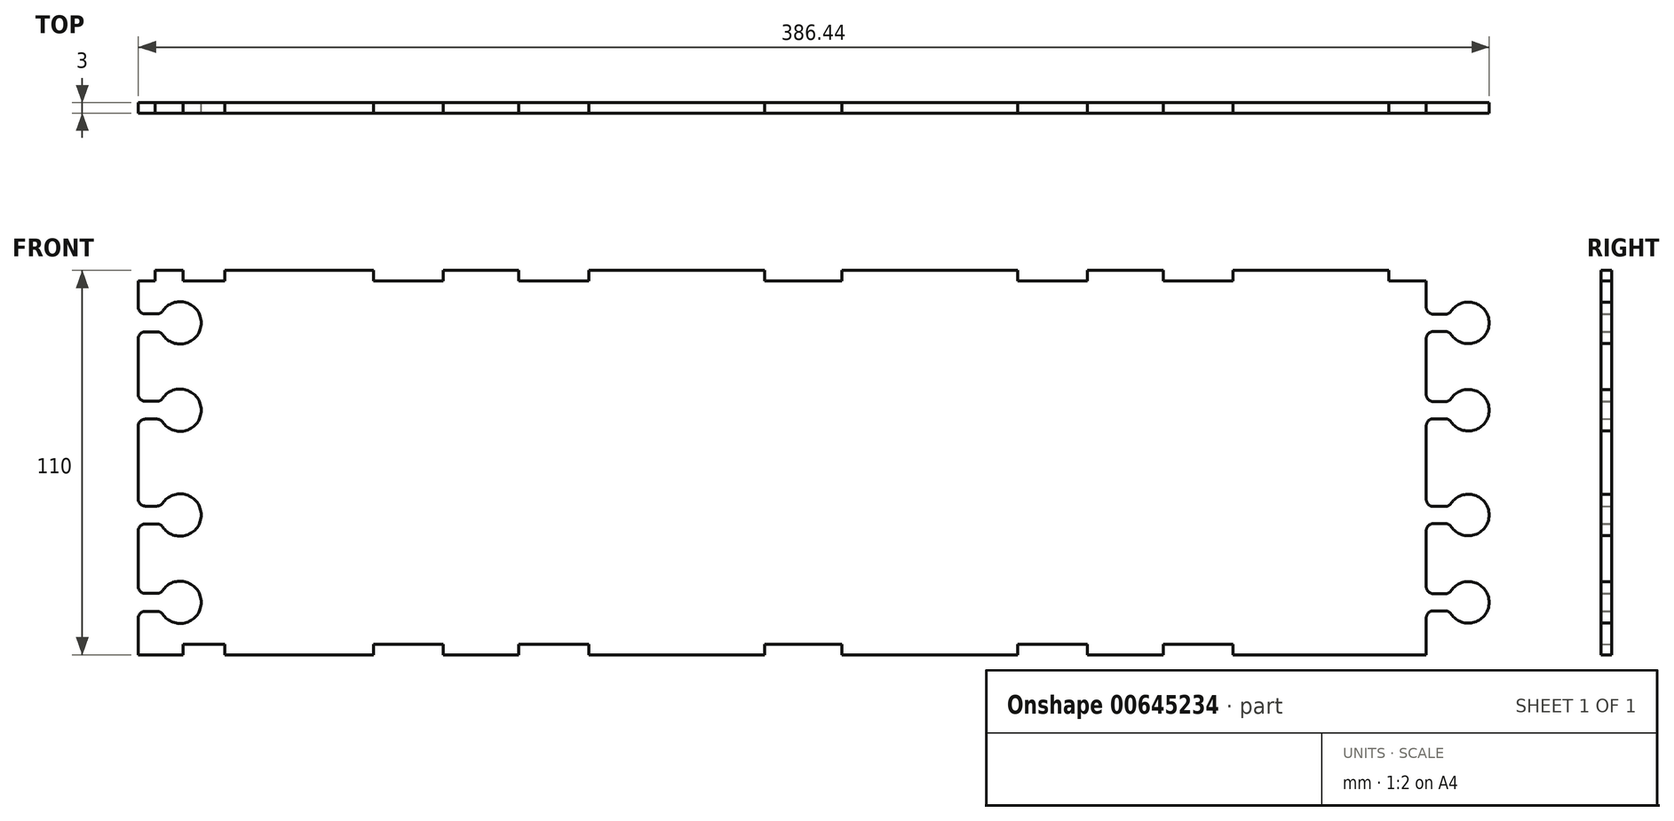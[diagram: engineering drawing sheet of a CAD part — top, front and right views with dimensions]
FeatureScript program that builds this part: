
annotation { "Feature Type Name" : "Feature", "Feature Type Description" : "" }
export const myFeature = defineFeature(function(context is Context, id is Id, definition is map)
    precondition{}
    {
        {
            var Q0;
            Q0=qCreatedBy(makeId("Front.planeOp"),FACE);
            var sketch = newSketch(context, id + "F0", { "sketchPlane" : qUnion([Q0])});
            skLineSegment(sketch, "E0", {"start": v(142.7, 55) * mm, "end": v(142.7, -55) * mm});
            skLineSegment(sketch, "E1", {"start": v(52.34, 55) * mm, "end": v(18.8, 55) * mm});
            skLineSegment(sketch, "E2", {"start": v(18.8, 55) * mm, "end": v(18.8, -55) * mm});
            skLineSegment(sketch, "E3", {"start": v(18.8, -55) * mm, "end": v(52.34, -55) * mm});
            skLineSegment(sketch, "E4", {"start": v(-24.8, 55) * mm, "end": v(-58.34, 55) * mm});
            skLineSegment(sketch, "E5", {"start": v(159.47, 55) * mm, "end": v(125.94, 55) * mm});
            skLineSegment(sketch, "E6", {"start": v(-131.94, 55) * mm, "end": v(-165.47, 55) * mm});
            skLineSegment(sketch, "E7", {"start": v(-165.47, 55) * mm, "end": v(-165.47, -55) * mm});
            skLineSegment(sketch, "E8", {"start": v(-58.34, -55) * mm, "end": v(-24.8, -55) * mm});
            skLineSegment(sketch, "E9", {"start": v(-131.94, 55) * mm, "end": v(-131.94, -55) * mm});
            skLineSegment(sketch, "E10", {"start": v(125.94, 55) * mm, "end": v(125.94, -55) * mm});
            skLineSegment(sketch, "E11", {"start": v(-24.8, -55) * mm, "end": v(-14, -55) * mm});
            skLineSegment(sketch, "E12", {"start": v(159.47, 55) * mm, "end": v(159.47, -55) * mm});
            skLineSegment(sketch, "E13", {"start": v(52.34, 55) * mm, "end": v(52.34, -55) * mm});
            skLineSegment(sketch, "E14", {"start": v(8, -55) * mm, "end": v(8, -52) * mm});
            skLineSegment(sketch, "E15", {"start": v(-165.47, -55) * mm, "end": v(-131.94, -55) * mm});
            skLineSegment(sketch, "E16", {"start": v(8, 55) * mm, "end": v(18.8, 55) * mm});
            skLineSegment(sketch, "E17", {"start": v(-24.8, 55) * mm, "end": v(-24.8, -55) * mm});
            skLineSegment(sketch, "E18", {"start": v(-14, 52) * mm, "end": v(8, 52) * mm});
            skLineSegment(sketch, "E19", {"start": v(-14, 55) * mm, "end": v(-14, 52) * mm});
            skLineSegment(sketch, "E20", {"start": v(8, -52) * mm, "end": v(-14, -52) * mm});
            skLineSegment(sketch, "E21", {"start": v(-58.34, 55) * mm, "end": v(-58.34, -55) * mm});
            skLineSegment(sketch, "E22", {"start": v(-125.94, -52) * mm, "end": v(-125.94, -55) * mm});
            skLineSegment(sketch, "E23", {"start": v(8, 52) * mm, "end": v(8, 55) * mm});
            skLineSegment(sketch, "E24", {"start": v(-105.94, -52) * mm, "end": v(-125.94, -52) * mm});
            skLineSegment(sketch, "E25", {"start": v(-105.94, -55) * mm, "end": v(-105.94, -52) * mm});
            skLineSegment(sketch, "E26", {"start": v(-105.94, -55) * mm, "end": v(-84.34, -55) * mm});
            skLineSegment(sketch, "E27", {"start": v(-24.8, 55) * mm, "end": v(-14, 55) * mm});
            skLineSegment(sketch, "E28", {"start": v(-131.94, 55) * mm, "end": v(-125.94, 55) * mm});
            skLineSegment(sketch, "E29", {"start": v(8, -55) * mm, "end": v(18.8, -55) * mm});
            skLineSegment(sketch, "E30", {"start": v(125.94, -55) * mm, "end": v(159.47, -55) * mm});
            skLineSegment(sketch, "E31", {"start": v(-64.34, 55) * mm, "end": v(-58.34, 55) * mm});
            skLineSegment(sketch, "E32", {"start": v(-14, -52) * mm, "end": v(-14, -55) * mm});
            skLineSegment(sketch, "E33", {"start": v(-64.34, -52) * mm, "end": v(-84.34, -52) * mm});
            skLineSegment(sketch, "E34", {"start": v(-84.34, 55) * mm, "end": v(-84.34, 52) * mm});
            skLineSegment(sketch, "E35", {"start": v(-131.94, -55) * mm, "end": v(-125.94, -55) * mm});
            skLineSegment(sketch, "E36", {"start": v(-64.34, -55) * mm, "end": v(-64.34, -52) * mm});
            skLineSegment(sketch, "E37", {"start": v(-64.34, 52) * mm, "end": v(-64.34, 55) * mm});
            skLineSegment(sketch, "E38", {"start": v(164.47, 55) * mm, "end": v(164.47, 52) * mm});
            skLineSegment(sketch, "E39", {"start": v(-84.34, -52) * mm, "end": v(-84.34, -55) * mm});
            skLineSegment(sketch, "E40", {"start": v(-105.94, 55) * mm, "end": v(-84.34, 55) * mm});
            skLineSegment(sketch, "E41", {"start": v(175.22, -55) * mm, "end": v(175.22, -44.5) * mm});
            skLineSegment(sketch, "E42", {"start": v(-64.34, -55) * mm, "end": v(-58.34, -55) * mm});
            skLineSegment(sketch, "E43", {"start": v(-125.94, 52) * mm, "end": v(-105.94, 52) * mm});
            skArc(sketch, "E44", {"start": v(175.22, -44.5) * mm, "mid": v(175.82, -43.05) * mm, "end": v(177.27, -42.45) * mm});
            skLineSegment(sketch, "E45", {"start": v(-84.34, 52) * mm, "end": v(-64.34, 52) * mm});
            skArc(sketch, "E46", {"start": v(182.35, -36.65) * mm, "mid": v(193.22, -40) * mm, "end": v(182.35, -43.35) * mm});
            skLineSegment(sketch, "E47", {"start": v(159.47, 55) * mm, "end": v(164.47, 55) * mm});
            skLineSegment(sketch, "E48", {"start": v(-105.94, 52) * mm, "end": v(-105.94, 55) * mm});
            skLineSegment(sketch, "E49", {"start": v(177.27, -42.45) * mm, "end": v(180.66, -42.45) * mm});
            skLineSegment(sketch, "E50", {"start": v(175.22, -35.5) * mm, "end": v(175.22, -19.5) * mm});
            skLineSegment(sketch, "E51", {"start": v(-125.94, 55) * mm, "end": v(-125.94, 52) * mm});
            skArc(sketch, "E52", {"start": v(175.22, -19.5) * mm, "mid": v(175.82, -18.05) * mm, "end": v(177.27, -17.45) * mm});
            skArc(sketch, "E53", {"start": v(182.35, -36.65) * mm, "mid": v(181.62, -37.31) * mm, "end": v(180.66, -37.55) * mm});
            skArc(sketch, "E54", {"start": v(182.35, -11.65) * mm, "mid": v(193.22, -15) * mm, "end": v(182.35, -18.35) * mm});
            skLineSegment(sketch, "E55", {"start": v(180.66, -37.55) * mm, "end": v(177.27, -37.55) * mm});
            skLineSegment(sketch, "E56", {"start": v(180.66, -12.55) * mm, "end": v(177.27, -12.55) * mm});
            skLineSegment(sketch, "E57", {"start": v(177.27, -17.45) * mm, "end": v(180.66, -17.45) * mm});
            skLineSegment(sketch, "E58", {"start": v(159.47, -55) * mm, "end": v(175.22, -55) * mm});
            skArc(sketch, "E59", {"start": v(177.27, 12.55) * mm, "mid": v(175.82, 11.95) * mm, "end": v(175.22, 10.5) * mm});
            skArc(sketch, "E60", {"start": v(180.66, -17.45) * mm, "mid": v(181.62, -17.69) * mm, "end": v(182.35, -18.35) * mm});
            skArc(sketch, "E61", {"start": v(182.35, -11.65) * mm, "mid": v(181.62, -12.31) * mm, "end": v(180.66, -12.55) * mm});
            skArc(sketch, "E62", {"start": v(177.27, -37.55) * mm, "mid": v(175.82, -36.95) * mm, "end": v(175.22, -35.5) * mm});
            skArc(sketch, "E63", {"start": v(177.27, -12.55) * mm, "mid": v(175.82, -11.95) * mm, "end": v(175.22, -10.5) * mm});
            skLineSegment(sketch, "E64", {"start": v(175.22, -10.5) * mm, "end": v(175.22, 10.5) * mm});
            skArc(sketch, "E65", {"start": v(175.22, 19.5) * mm, "mid": v(175.82, 18.05) * mm, "end": v(177.27, 17.45) * mm});
            skLineSegment(sketch, "E66", {"start": v(175.22, 19.5) * mm, "end": v(175.22, 35.5) * mm});
            skArc(sketch, "E67", {"start": v(182.35, 11.65) * mm, "mid": v(181.62, 12.31) * mm, "end": v(180.66, 12.55) * mm});
            skLineSegment(sketch, "E68", {"start": v(180.66, 37.55) * mm, "end": v(177.27, 37.55) * mm});
            skArc(sketch, "E69", {"start": v(180.66, 17.45) * mm, "mid": v(181.62, 17.69) * mm, "end": v(182.35, 18.35) * mm});
            skArc(sketch, "E70", {"start": v(180.66, -42.45) * mm, "mid": v(181.62, -42.69) * mm, "end": v(182.35, -43.35) * mm});
            skLineSegment(sketch, "E71", {"start": v(177.27, 17.45) * mm, "end": v(180.66, 17.45) * mm});
            skArc(sketch, "E72", {"start": v(182.35, 36.65) * mm, "mid": v(181.62, 37.31) * mm, "end": v(180.66, 37.55) * mm});
            skArc(sketch, "E73", {"start": v(182.35, 36.65) * mm, "mid": v(193.22, 40) * mm, "end": v(182.35, 43.35) * mm});
            skArc(sketch, "E74", {"start": v(180.66, 42.45) * mm, "mid": v(181.62, 42.69) * mm, "end": v(182.35, 43.35) * mm});
            skArc(sketch, "E75", {"start": v(175.22, 44.5) * mm, "mid": v(175.82, 43.05) * mm, "end": v(177.27, 42.45) * mm});
            skArc(sketch, "E76", {"start": v(177.27, 37.55) * mm, "mid": v(175.82, 36.95) * mm, "end": v(175.22, 35.5) * mm});
            skArc(sketch, "E77", {"start": v(182.35, 11.65) * mm, "mid": v(193.22, 15) * mm, "end": v(182.35, 18.35) * mm});
            skLineSegment(sketch, "E78", {"start": v(164.47, 52) * mm, "end": v(175.22, 52) * mm});
            skLineSegment(sketch, "E79", {"start": v(78.34, 52) * mm, "end": v(78.34, 55) * mm});
            skLineSegment(sketch, "E80", {"start": v(58.34, 52) * mm, "end": v(78.34, 52) * mm});
            skLineSegment(sketch, "E81", {"start": v(175.22, 44.5) * mm, "end": v(175.22, 52) * mm});
            skLineSegment(sketch, "E82", {"start": v(52.34, 55) * mm, "end": v(58.34, 55) * mm});
            skLineSegment(sketch, "E83", {"start": v(52.34, -55) * mm, "end": v(58.34, -55) * mm});
            skLineSegment(sketch, "E84", {"start": v(180.66, 12.55) * mm, "end": v(177.27, 12.55) * mm});
            skLineSegment(sketch, "E85", {"start": v(99.94, -52) * mm, "end": v(99.94, -55) * mm});
            skLineSegment(sketch, "E86", {"start": v(119.94, -52) * mm, "end": v(99.94, -52) * mm});
            skLineSegment(sketch, "E87", {"start": v(119.94, -55) * mm, "end": v(119.94, -52) * mm});
            skLineSegment(sketch, "E88", {"start": v(119.94, -55) * mm, "end": v(125.94, -55) * mm});
            skLineSegment(sketch, "E89", {"start": v(78.34, -52) * mm, "end": v(58.34, -52) * mm});
            skLineSegment(sketch, "E90", {"start": v(78.34, -55) * mm, "end": v(78.34, -52) * mm});
            skLineSegment(sketch, "E91", {"start": v(119.94, 52) * mm, "end": v(119.94, 55) * mm});
            skLineSegment(sketch, "E92", {"start": v(99.94, 52) * mm, "end": v(119.94, 52) * mm});
            skLineSegment(sketch, "E93", {"start": v(58.34, 55) * mm, "end": v(58.34, 52) * mm});
            skLineSegment(sketch, "E94", {"start": v(58.34, -52) * mm, "end": v(58.34, -55) * mm});
            skLineSegment(sketch, "E95", {"start": v(119.94, 55) * mm, "end": v(125.94, 55) * mm});
            skLineSegment(sketch, "E96", {"start": v(-191.27, 42.55) * mm, "end": v(-187.89, 42.55) * mm});
            skLineSegment(sketch, "E97", {"start": v(78.34, 55) * mm, "end": v(99.94, 55) * mm});
            skLineSegment(sketch, "E98", {"start": v(99.94, 55) * mm, "end": v(99.94, 52) * mm});
            skLineSegment(sketch, "E99", {"start": v(177.27, 42.45) * mm, "end": v(180.66, 42.45) * mm});
            skLineSegment(sketch, "E100", {"start": v(-193.22, 52) * mm, "end": v(-188.47, 52) * mm});
            skLineSegment(sketch, "E101", {"start": v(-193.22, 44.5) * mm, "end": v(-193.22, 52) * mm});
            skArc(sketch, "E102", {"start": v(-191.27, 37.45) * mm, "mid": v(-192.65, 36.88) * mm, "end": v(-193.22, 35.5) * mm});
            skLineSegment(sketch, "E103", {"start": v(-193.22, 19.5) * mm, "end": v(-193.22, 35.5) * mm});
            skLineSegment(sketch, "E104", {"start": v(78.34, -55) * mm, "end": v(99.94, -55) * mm});
            skArc(sketch, "E105", {"start": v(-186.28, 36.6) * mm, "mid": v(-175.22, 40) * mm, "end": v(-186.28, 43.4) * mm});
            skArc(sketch, "E106", {"start": v(-187.89, 17.55) * mm, "mid": v(-186.98, 17.78) * mm, "end": v(-186.28, 18.4) * mm});
            skArc(sketch, "E107", {"start": v(-186.28, 11.6) * mm, "mid": v(-175.22, 15) * mm, "end": v(-186.28, 18.4) * mm});
            skLineSegment(sketch, "E108", {"start": v(-187.89, 37.45) * mm, "end": v(-191.27, 37.45) * mm});
            skArc(sketch, "E109", {"start": v(-193.22, 44.5) * mm, "mid": v(-192.65, 43.12) * mm, "end": v(-191.27, 42.55) * mm});
            skArc(sketch, "E110", {"start": v(-191.27, 12.45) * mm, "mid": v(-192.65, 11.88) * mm, "end": v(-193.22, 10.5) * mm});
            skLineSegment(sketch, "E111", {"start": v(-193.22, -10.5) * mm, "end": v(-193.22, 10.5) * mm});
            skArc(sketch, "E112", {"start": v(-186.28, 36.6) * mm, "mid": v(-186.98, 37.22) * mm, "end": v(-187.89, 37.45) * mm});
            skArc(sketch, "E113", {"start": v(-186.28, 11.6) * mm, "mid": v(-186.98, 12.22) * mm, "end": v(-187.89, 12.45) * mm});
            skArc(sketch, "E114", {"start": v(-186.28, -11.6) * mm, "mid": v(-175.22, -15) * mm, "end": v(-186.28, -18.4) * mm});
            skArc(sketch, "E115", {"start": v(-187.89, -17.55) * mm, "mid": v(-186.98, -17.78) * mm, "end": v(-186.28, -18.4) * mm});
            skArc(sketch, "E116", {"start": v(-193.22, 19.5) * mm, "mid": v(-192.65, 18.12) * mm, "end": v(-191.27, 17.55) * mm});
            skArc(sketch, "E117", {"start": v(-187.89, 42.55) * mm, "mid": v(-186.98, 42.78) * mm, "end": v(-186.28, 43.4) * mm});
            skArc(sketch, "E118", {"start": v(-193.22, -19.5) * mm, "mid": v(-192.65, -18.12) * mm, "end": v(-191.27, -17.55) * mm});
            skArc(sketch, "E119", {"start": v(-191.27, -12.45) * mm, "mid": v(-192.65, -11.88) * mm, "end": v(-193.22, -10.5) * mm});
            skArc(sketch, "E120", {"start": v(-191.27, -37.45) * mm, "mid": v(-192.65, -36.88) * mm, "end": v(-193.22, -35.5) * mm});
            skLineSegment(sketch, "E121", {"start": v(-187.89, 12.45) * mm, "end": v(-191.27, 12.45) * mm});
            skArc(sketch, "E122", {"start": v(-186.28, -36.6) * mm, "mid": v(-186.98, -37.22) * mm, "end": v(-187.89, -37.45) * mm});
            skLineSegment(sketch, "E123", {"start": v(-191.27, -17.55) * mm, "end": v(-187.89, -17.55) * mm});
            skLineSegment(sketch, "E124", {"start": v(-193.22, -35.5) * mm, "end": v(-193.22, -19.5) * mm});
            skLineSegment(sketch, "E125", {"start": v(-187.89, -12.45) * mm, "end": v(-191.27, -12.45) * mm});
            skLineSegment(sketch, "E126", {"start": v(-187.89, -37.45) * mm, "end": v(-191.27, -37.45) * mm});
            skLineSegment(sketch, "E127", {"start": v(-193.22, -55) * mm, "end": v(-193.22, -44.5) * mm});
            skLineSegment(sketch, "E128", {"start": v(-193.22, -55) * mm, "end": v(-180.47, -55) * mm});
            skArc(sketch, "E129", {"start": v(-186.28, -11.6) * mm, "mid": v(-186.98, -12.22) * mm, "end": v(-187.89, -12.45) * mm});
            skArc(sketch, "E130", {"start": v(-187.89, -42.55) * mm, "mid": v(-186.98, -42.78) * mm, "end": v(-186.28, -43.4) * mm});
            skLineSegment(sketch, "E131", {"start": v(-191.27, -42.55) * mm, "end": v(-187.89, -42.55) * mm});
            skArc(sketch, "E132", {"start": v(-193.22, -44.5) * mm, "mid": v(-192.65, -43.12) * mm, "end": v(-191.27, -42.55) * mm});
            skLineSegment(sketch, "E133", {"start": v(-180.47, -52) * mm, "end": v(-180.47, -55) * mm});
            skLineSegment(sketch, "E134", {"start": v(-191.27, 17.55) * mm, "end": v(-187.89, 17.55) * mm});
            skLineSegment(sketch, "E135", {"start": v(-168.47, -52) * mm, "end": v(-180.47, -52) * mm});
            skArc(sketch, "E136", {"start": v(-186.28, -36.6) * mm, "mid": v(-175.22, -40) * mm, "end": v(-186.28, -43.4) * mm});
            skLineSegment(sketch, "E137", {"start": v(-168.47, -55) * mm, "end": v(-168.47, -52) * mm});
            skLineSegment(sketch, "E138", {"start": v(-188.47, 52) * mm, "end": v(-188.47, 55) * mm});
            skLineSegment(sketch, "E139", {"start": v(-168.47, -55) * mm, "end": v(-165.47, -55) * mm});
            skLineSegment(sketch, "E140", {"start": v(-168.47, 52) * mm, "end": v(-168.47, 55) * mm});
            skLineSegment(sketch, "E141", {"start": v(-180.47, 52) * mm, "end": v(-168.47, 52) * mm});
            skLineSegment(sketch, "E142", {"start": v(-180.47, 55) * mm, "end": v(-180.47, 52) * mm});
            skLineSegment(sketch, "E143", {"start": v(-188.47, 55) * mm, "end": v(-180.47, 55) * mm});
            skLineSegment(sketch, "E144", {"start": v(-168.47, 55) * mm, "end": v(-165.47, 55) * mm});
            skLineSegment(sketch, "E145", {"start": v(-148.7, 55) * mm, "end": v(-148.7, -55) * mm});
            skLineSegment(sketch, "E146", {"start": v(35.57, 55) * mm, "end": v(35.57, -55) * mm});
            skLineSegment(sketch, "E147", {"start": v(-41.57, 55) * mm, "end": v(-41.57, -55) * mm});
            skSolve(sketch);
        }
        {
            var Q0;
            Q0=makeQuery(id+"F0.imprint","IMPRINT",FACE,{"disambiguationData":[TD([[makeQuery(id+"F0.imprint","IMPRINT",EDGE,{"derivedFrom":sQuery(id+"F0.wireOp",EDGE,"E7")}),-1.0]])]});
            var Q1;
            {var subQ0=sQuery(id+"F0.wireOp",EDGE,"E7");Q1=makeQuery(id+"F0.imprint","IMPRINT",FACE,{"disambiguationData":[TD([[makeQuery(id+"F0.imprint","IMPRINT",EDGE,{"derivedFrom":subQ0}),1.0]])]});}
            var Q2;
            {var subQ0=sQuery(id+"F0.wireOp",EDGE,"E9");Q2=makeQuery(id+"F0.imprint","IMPRINT",FACE,{"disambiguationData":[TD([[makeQuery(id+"F0.imprint","IMPRINT",EDGE,{"derivedFrom":subQ0}),-1.0]])]});}
            var Q3;
            Q3=makeQuery(id+"F0.imprint","IMPRINT",FACE,{"disambiguationData":[TD([[makeQuery(id+"F0.imprint","IMPRINT",EDGE,{"derivedFrom":sQuery(id+"F0.wireOp",EDGE,"E9")}),1.0]])]});
            var Q4;
            {var subQ0=sQuery(id+"F0.wireOp",EDGE,"E17");Q4=makeQuery(id+"F0.imprint","IMPRINT",FACE,{"disambiguationData":[TD([[makeQuery(id+"F0.imprint","IMPRINT",EDGE,{"derivedFrom":subQ0}),-1.0]])]});}
            var Q5;
            Q5=makeQuery(id+"F0.imprint","IMPRINT",FACE,{"disambiguationData":[TD([[makeQuery(id+"F0.imprint","IMPRINT",EDGE,{"derivedFrom":sQuery(id+"F0.wireOp",EDGE,"E2")}),-1.0]])]});
            var Q6;
            {var subQ0=sQuery(id+"F0.wireOp",EDGE,"E2");Q6=makeQuery(id+"F0.imprint","IMPRINT",FACE,{"disambiguationData":[TD([[makeQuery(id+"F0.imprint","IMPRINT",EDGE,{"derivedFrom":subQ0}),1.0]])]});}
            var Q7;
            {var subQ0=sQuery(id+"F0.wireOp",EDGE,"E13");Q7=makeQuery(id+"F0.imprint","IMPRINT",FACE,{"disambiguationData":[TD([[makeQuery(id+"F0.imprint","IMPRINT",EDGE,{"derivedFrom":subQ0}),-1.0]])]});}
            var Q8;
            Q8=makeQuery(id+"F0.imprint","IMPRINT",FACE,{"disambiguationData":[TD([[makeQuery(id+"F0.imprint","IMPRINT",EDGE,{"derivedFrom":sQuery(id+"F0.wireOp",EDGE,"E10")}),-1.0]])]});
            var Q9;
            {var subQ0=sQuery(id+"F0.wireOp",EDGE,"E0");Q9=makeQuery(id+"F0.imprint","IMPRINT",FACE,{"disambiguationData":[TD([[makeQuery(id+"F0.imprint","IMPRINT",EDGE,{"derivedFrom":subQ0}),-1.0]])]});}
            var Q10;
            {var subQ0=sQuery(id+"F0.wireOp",EDGE,"E0");Q10=makeQuery(id+"F0.imprint","IMPRINT",FACE,{"disambiguationData":[TD([[makeQuery(id+"F0.imprint","IMPRINT",EDGE,{"derivedFrom":subQ0}),1.0]])]});}
            var Q11;
            Q11=makeQuery(id+"F0.imprint","IMPRINT",FACE,{"disambiguationData":[TD([[makeQuery(id+"F0.imprint","IMPRINT",EDGE,{"derivedFrom":sQuery(id+"F0.wireOp",EDGE,"E12")}),1.0]])]});
            var Q12;
            {var subQ0=sQuery(id+"F0.wireOp",EDGE,"E21");Q12=makeQuery(id+"F0.imprint","IMPRINT",FACE,{"disambiguationData":[TD([[makeQuery(id+"F0.imprint","IMPRINT",EDGE,{"derivedFrom":subQ0}),1.0]])]});}
            extrude(context, id + "F1", {"entities" : qUnion([Q0, Q1, Q2, Q3, Q4, Q5, Q6, Q7, Q8, Q9, Q10, Q11, Q12]), "depth" : 3 * mm, "offsetDistance" : 25 * mm});
        }
    });
